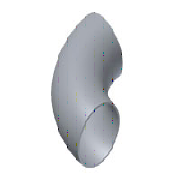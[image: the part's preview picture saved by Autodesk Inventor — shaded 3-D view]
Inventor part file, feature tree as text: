
AUTODESK INVENTOR PART (.ipt)
format: ipt  version: 2023.2 (Build 272271030, 271C)  size: 179,712 bytes
history: native  units: mm
features: other x4, sketch x2, sweep x1
ambient origin geometry x8: Origin, YZ Plane, XZ Plane, XY Plane, X Axis, Y Axis, Z Axis, Center Point
bodies: Solid1 (feature_tree)
feature tree (7):
  sweep  "Sweep1"
  other  "Work Axis1"
  other  "Work Axis2"
  sketch  "Sketch1"  dims[d2=114.0mm d3=6.0mm]
  sketch  "Sketch2"  dims[d4=150.0mm d5=300.0mm d6=0.0mm d7=90.0deg d8=0.0mm]
  other  "Work Point1"
  other  "Work Point2"
